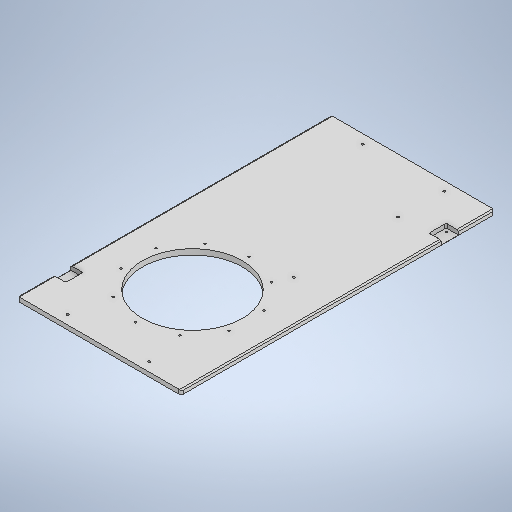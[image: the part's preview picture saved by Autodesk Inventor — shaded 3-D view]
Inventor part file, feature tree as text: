
AUTODESK INVENTOR PART (.ipt)
format: ipt  version: 2025 (Build 290162000, 162)  size: 442,880 bytes
history: native  units: in
note: dims shown in document units (in); Inventor stores cm internally (conversion verified against a paired STEP export)
features: sketch x10, extrude x5, hole x4, chamfer x3, plane x2, fillet x2, pattern_circular x1
ambient origin geometry x8: Origin, YZ Plane, XZ Plane, XY Plane, X Axis, Y Axis, Z Axis, Center Point
bodies: Solid1 (feature_tree)
feature tree (27):
  extrude  "Base Cover"  Depth=27.1654in
  sketch  "Sketch2"  dims[d2=0.4724in d3=0.0in d4=8.0709in]
  extrude  "Cylinder Hole"  Depth=0.4724in
  plane  "Work Plane1"
  hole  "Handle Holes"  [1 undecoded]
  sketch  "Sketch7"  dims[d8=10.6299in d50=5.9055in d55=7.0625in]
  plane  "Work Plane2"
  hole  "Cylinder Mount Holes"  [1 undecoded]
  sketch  "Sketch9"  dims[d57=0.1936in d58=0.1969in d59=0.1575in d60=0.0787in d61=90.0deg d62=0.1969in d63=0.8108in]
  fillet  "Rounded Side Corners"  Radius=7.0625in
  chamfer  "Chamfer1"  Distance=1.063in
  chamfer  "Chamfer2"  Distance=1.063in
  extrude  "Magnet Seats"  Depth=0.315in
  hole  "Magnet Holes"  [1 undecoded]
  chamfer  "Chamfer5"  Distance=3.1102in
  fillet  "Rounded Bottom Corners"  Radius=3.1102in
  extrude  "Extrusion14"  Depth=0.315in
  extrude  "Extrusion15"  Depth=0.0984in TaperAngle=45.0deg
  pattern_circular  "Circular Pattern1"  Angle=45.0deg  [1 undecoded]
  hole  "LV Beam Feet Holes"  [1 undecoded]
  sketch  "Sketch1"  dims[d0=14.1732in d1=27.1654in]
  sketch  "Sketch6"  dims[d5=8.6614in d6=0.0in d7=0.0in]
  sketch  "Sketch8"  dims[d56=25.5906in]
  sketch  "Sketch11"  dims[d64=10.3543in]
  sketch  "Sketch18"  dims[d65=10.6299in]
  sketch  "Sketch19"  dims[d68=9.8425in]
  sketch  "Sketch22"  dims[d74=0.1628in d75=0.3937in d76=0.1575in d77=0.0787in d78=90.0deg d79=0.3937in d80=0.8108in d82=1.063in d83=1.063in d84=1.4961in d85=1.4961in d86=3.1102in d87=3.1102in d88=0.1969in d89=0.0984in d90=0.0787in d91=45.0deg d92=0.0984in d93=0.0787in d94=45.0deg d95=0.1181in d96=0.1181in d97=0.3543in d98=0.0in d109=0.748in d110=0.315in d111=0.8661in d112=0.748in d113=0.1299in d114=0.1299in d115=0.1299in d116=0.1299in d118=0.315in d119=0.8661in d120=0.748in d121=0.748in d122=0.1276in d123=0.315in d124=0.1575in d125=0.0787in d126=90.0deg d127=0.315in d128=0.8108in d129=0.0138in d130=0.0787in d131=45.0deg d230=0.2756in d243=0.1378in d244=0.0787in d245=0.3848in d246=0.0in d247=0.1378in d248=0.0787in d249=0.3937in d250=0.0in d278=0.1575in d279=3.937in d280=360.0deg d284=0.1969in d285=0.2362in d286=0.1575in d287=0.0787in d288=90.0deg d289=0.315in d290=0.0in d291=13.3858in d292=3.622in d293=3.622in d294=4.7244in d26=0.0394in d27=0.0394in d28=0.0394in d29=0.0059in d30=0.0098in d31=0.0148in d32=0.5635in d33=0.0295in d34=0.8108in d35=0.0025in d36=0.0295in d37=0.0148in d66=0.0197in d67=0.0344in d251=0.0394in d252=0.0394in d253=0.0394in d254=0.0059in d255=0.0098in d256=0.0148in d257=0.5635in d258=0.0295in d259=0.8108in d260=0.0025in d261=0.0295in d262=0.0148in d263=0.0394in d264=0.0394in d265=0.0059in d266=0.0098in d267=0.0148in d268=0.5635in d269=0.0295in d270=0.8108in d271=0.0025in d272=0.0295in d273=0.0148in]
note: 5 required parameter values undecoded (feature->parameter linkage not recoverable at this tier; creation-order binding heuristic only, values carry confidence <= 0.55)
